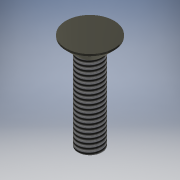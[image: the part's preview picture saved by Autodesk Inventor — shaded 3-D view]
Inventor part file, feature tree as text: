
AUTODESK INVENTOR PART (.ipt)
format: ipt  version: 2016 (Build 200138000, 138)  size: 129,024 bytes
history: native  units: mm
features: extrude x3, sketch x3, other x1, thread x1, chamfer x1
ambient origin geometry x1: Origin
bodies: Body1 (feature_tree)
feature tree (9):
  other  "ソリッド1"
  extrude  "押し出し1"  Depth=4.0mm
  extrude  "押し出し2"  Depth=6.0mm TaperAngle=0.0deg
  thread  "ねじ1"
  chamfer  "面取り1"  Distance=8.0mm
  extrude  "押し出し4"  Depth=2.3mm TaperAngle=0.0deg
  sketch  "スケッチ1"
  sketch  "スケッチ2"
  sketch  "スケッチ4"
